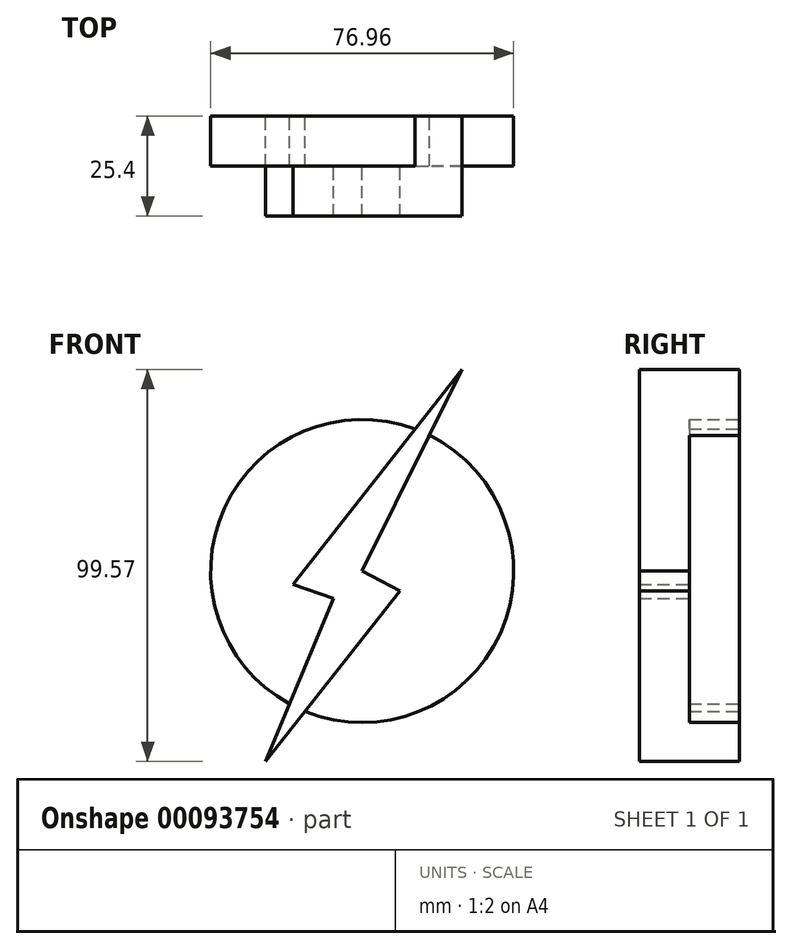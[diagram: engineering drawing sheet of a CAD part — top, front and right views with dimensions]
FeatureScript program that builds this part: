
annotation { "Feature Type Name" : "Feature", "Feature Type Description" : "" }
export const myFeature = defineFeature(function(context is Context, id is Id, definition is map)
    precondition{}
    {
        {
            var Q0;
            Q0=qCreatedBy(makeId("Front.planeOp"),FACE);
            var sketch = newSketch(context, id + "F0", { "sketchPlane" : qUnion([Q0])});
            skCircle(sketch, "E0", {"center": v(0, 0) * mm, "radius": 36 * mm});
            skLineSegment(sketch, "E1", {"start": v(0, 0) * mm, "end": v(25.3, 51.2) * mm});
            skLineSegment(sketch, "E2", {"start": v(25.3, 51.2) * mm, "end": v(-17.57, -3.4) * mm});
            skLineSegment(sketch, "E3", {"start": v(-17.57, -3.4) * mm, "end": v(-7.26, -6.91) * mm});
            skLineSegment(sketch, "E4", {"start": v(-7.26, -6.91) * mm, "end": v(-24.6, -48.38) * mm});
            skLineSegment(sketch, "E5", {"start": v(-24.6, -48.38) * mm, "end": v(9.6, -5.04) * mm});
            skLineSegment(sketch, "E6", {"start": v(9.6, -5.04) * mm, "end": v(0, 0) * mm});
            skSolve(sketch);
        }
        {
            var Q0;
            {var subQ0=sQuery(id+"F0.wireOp",EDGE,"E3");Q0=makeQuery(id+"F0.imprint","IMPRINT",FACE,{"disambiguationData":[TD([[makeQuery(id+"F0.imprint","IMPRINT",EDGE,{"derivedFrom":subQ0}),1.0]])]});}
            var Q1;
            {var subQ0=sQuery(id+"F0.wireOp",EDGE,"E4");var subQ1=sQuery(id+"F0.wireOp",EDGE,"E0");var subQ2=makeQuery(id+"F0.imprint","INTERSECT",VERTEX,{"derivedFrom":[subQ1,subQ0]});Q1=makeQuery(id+"F0.imprint","IMPRINT",FACE,{"disambiguationData":[TD([[makeQuery(id+"F0.imprint","IMPRINT",EDGE,{"disambiguationData":[TD([[subQ2,-1.0]])],"derivedFrom":subQ1}),-1.0]])]});}
            var Q2;
            {var subQ0=sQuery(id+"F0.wireOp",EDGE,"E2");var subQ1=sQuery(id+"F0.wireOp",EDGE,"E0");var subQ2=makeQuery(id+"F0.imprint","INTERSECT",VERTEX,{"derivedFrom":[subQ1,subQ0]});Q2=makeQuery(id+"F0.imprint","IMPRINT",FACE,{"disambiguationData":[TD([[makeQuery(id+"F0.imprint","IMPRINT",EDGE,{"disambiguationData":[TD([[subQ2,1.0]])],"derivedFrom":subQ1}),-1.0]])]});}
            extrude(context, id + "F1", {"entities" : qUnion([Q0, Q1, Q2]), "depth" : 25.4 * mm});
        }
        {
            var Q0;
            Q0=qCreatedBy(makeId("Front.planeOp"),FACE);
            var sketch = newSketch(context, id + "F2", { "sketchPlane" : qUnion([Q0])});
            skCircle(sketch, "E7", {"center": v(0, 0) * mm, "radius": 38.48 * mm});
            skSolve(sketch);
        }
        {
            var Q0;
            Q0=makeQuery(id+"F2.imprint","IMPRINT",FACE,{"disambiguationData":[TD([[makeQuery(id+"F2.imprint","IMPRINT",EDGE,{"derivedFrom":sQuery(id+"F2.wireOp",EDGE,"E7")}),1.0]])]});
            extrude(context, id + "F3", {"entities" : qUnion([Q0]), "operationType" : NewBodyOperationType.ADD, "depth" : 12.7 * mm});
        }
    });
